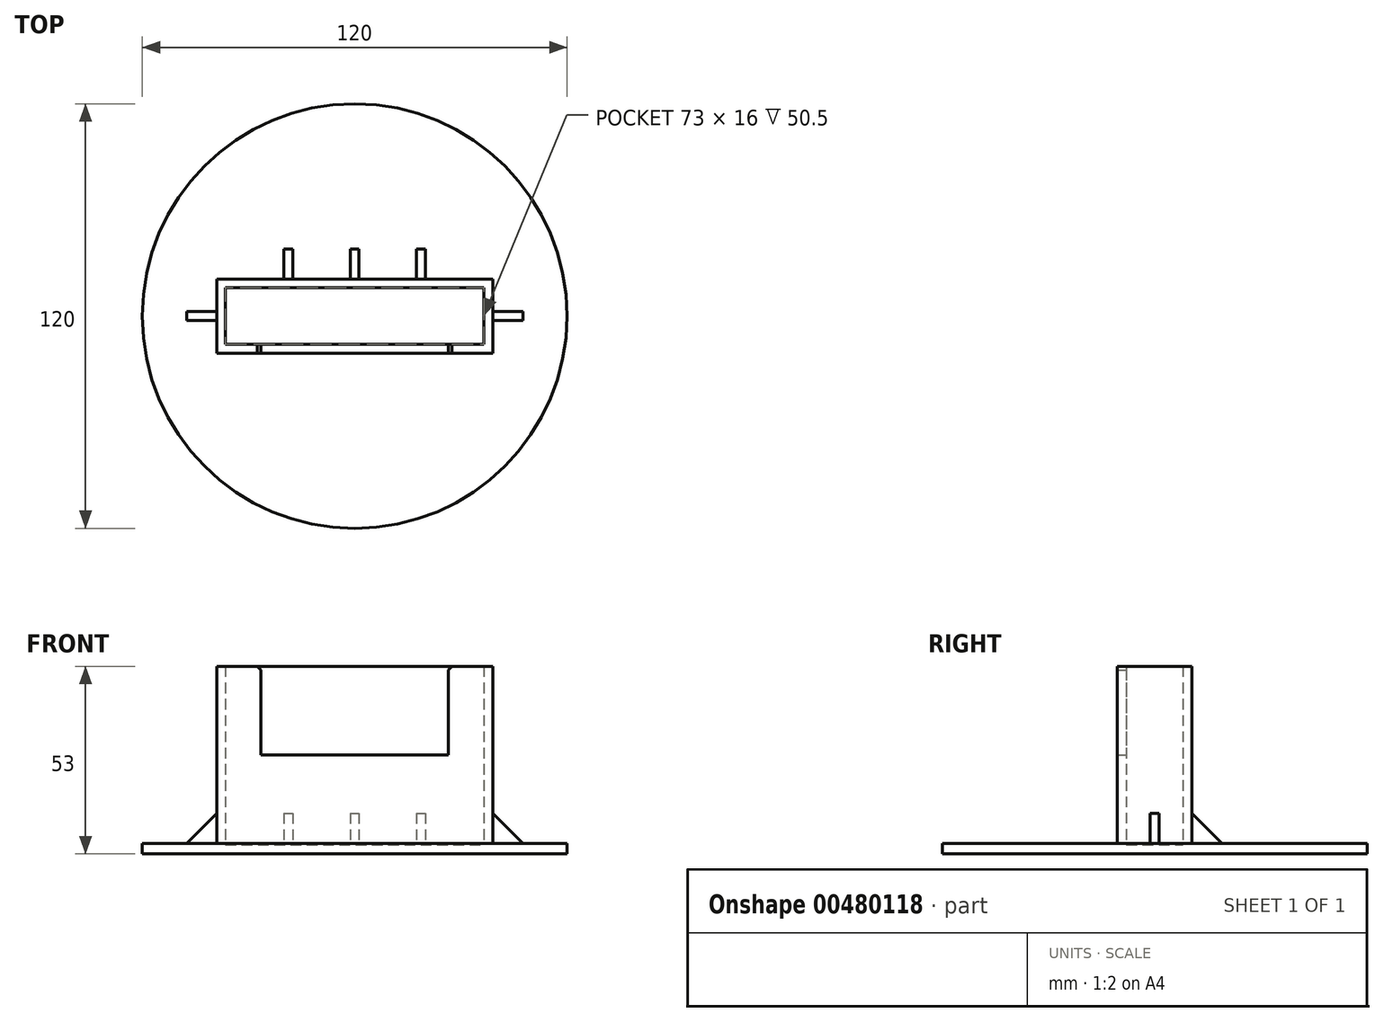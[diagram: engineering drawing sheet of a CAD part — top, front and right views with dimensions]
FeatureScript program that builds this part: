
annotation { "Feature Type Name" : "Feature", "Feature Type Description" : "" }
export const myFeature = defineFeature(function(context is Context, id is Id, definition is map)
    precondition{}
    {
        {
            var Q0;
            Q0=qCreatedBy(makeId("Top.planeOp"),FACE);
            var sketch = newSketch(context, id + "F0", { "sketchPlane" : qUnion([Q0])});
            skCircle(sketch, "E0", {"center": v(0, 0) * mm, "radius": 60 * mm});
            skLineSegment(sketch, "E1.bottom", {"start": v(39, 10.5) * mm, "end": v(-39, 10.5) * mm});
            skLineSegment(sketch, "E1.top", {"start": v(39, -10.5) * mm, "end": v(-39, -10.5) * mm});
            skLineSegment(sketch, "E1.left", {"start": v(39, 10.5) * mm, "end": v(39, -10.5) * mm});
            skLineSegment(sketch, "E1.right", {"start": v(-39, 10.5) * mm, "end": v(-39, -10.5) * mm});
            skPoint(sketch, "E2.endSnap0", {"position": v(0, 10.5) * mm});
            skPoint(sketch, "E3.endSnap0", {"position": v(39, 0) * mm});
            skLineSegment(sketch, "E4.0", {"start": v(-37.5, 1.25) * mm, "end": v(-47.5, 1.25) * mm});
            skLineSegment(sketch, "E5.0", {"start": v(-37.5, -1.25) * mm, "end": v(-47.5, -1.25) * mm});
            skLineSegment(sketch, "E6", {"start": v(-47.5, 1.25) * mm, "end": v(-47.5, -1.25) * mm});
            skLineSegment(sketch, "E7.0", {"start": v(-17.5, 9) * mm, "end": v(-17.5, 19) * mm});
            skLineSegment(sketch, "E8.0", {"start": v(-20, 9) * mm, "end": v(-20, 19) * mm});
            skLineSegment(sketch, "E9.0", {"start": v(1.25, 9) * mm, "end": v(1.25, 19) * mm});
            skLineSegment(sketch, "E10.0", {"start": v(-1.25, 9) * mm, "end": v(-1.25, 19) * mm});
            skLineSegment(sketch, "E11.0", {"start": v(20, 9) * mm, "end": v(20, 19) * mm});
            skLineSegment(sketch, "E12.0", {"start": v(17.5, 9) * mm, "end": v(17.5, 19) * mm});
            skLineSegment(sketch, "E13.0", {"start": v(37.5, -1.25) * mm, "end": v(47.5, -1.25) * mm});
            skLineSegment(sketch, "E14.0", {"start": v(37.5, 1.25) * mm, "end": v(47.5, 1.25) * mm});
            skLineSegment(sketch, "E15", {"start": v(-20, 19) * mm, "end": v(-17.5, 19) * mm});
            skLineSegment(sketch, "E16", {"start": v(-1.25, 19) * mm, "end": v(1.25, 19) * mm});
            skLineSegment(sketch, "E17", {"start": v(17.5, 19) * mm, "end": v(20, 19) * mm});
            skLineSegment(sketch, "E18", {"start": v(47.5, 1.25) * mm, "end": v(47.5, -1.25) * mm});
            skSolve(sketch);
        }
        {
            var Q0;
            Q0=qCreatedBy(makeId("Front.planeOp"),FACE);
            var sketch = newSketch(context, id + "F1", { "sketchPlane" : qUnion([Q0])});
            skPoint(sketch, "E19.middle", {"position": v(0, 0) * mm});
            skLineSegment(sketch, "E20", {"start": v(26.5, 25) * mm, "end": v(-26.5, 25) * mm});
            skLineSegment(sketch, "E21", {"start": v(-26.5, 25) * mm, "end": v(-26.5, 75) * mm});
            skLineSegment(sketch, "E22", {"start": v(26.5, 25) * mm, "end": v(26.5, 75) * mm});
            skLineSegment(sketch, "E23", {"start": v(-26.5, 75) * mm, "end": v(26.5, 75) * mm});
            skSolve(sketch);
        }
        {
            var Q0;
            Q0 = qSketchRegion(id + "F0", true);
            var Q1;
            Q1=makeQuery(id+"F0.imprint","IMPRINT",FACE,{"disambiguationData":[TD([[makeQuery(id+"F0.imprint","IMPRINT",EDGE,{"derivedFrom":sQuery(id+"F0.wireOp",EDGE,"E1.bottom")}),1.0]])]});
            var Q2;
            {var subQ0=sQuery(id+"F0.wireOp",EDGE,"E4.0");Q2=makeQuery(id+"F0.imprint","IMPRINT",FACE,{"disambiguationData":[TD([[makeQuery(id+"F0.imprint","IMPRINT",EDGE,{"derivedFrom":subQ0}),1.0]])]});}
            var Q3;
            {var subQ0=sQuery(id+"F0.wireOp",EDGE,"E7.0");Q3=makeQuery(id+"F0.imprint","IMPRINT",FACE,{"disambiguationData":[TD([[makeQuery(id+"F0.imprint","IMPRINT",EDGE,{"derivedFrom":subQ0}),1.0]])]});}
            var Q4;
            {var subQ0=sQuery(id+"F0.wireOp",EDGE,"E9.0");Q4=makeQuery(id+"F0.imprint","IMPRINT",FACE,{"disambiguationData":[TD([[makeQuery(id+"F0.imprint","IMPRINT",EDGE,{"derivedFrom":subQ0}),1.0]])]});}
            var Q5;
            {var subQ0=sQuery(id+"F0.wireOp",EDGE,"E11.0");Q5=makeQuery(id+"F0.imprint","IMPRINT",FACE,{"disambiguationData":[TD([[makeQuery(id+"F0.imprint","IMPRINT",EDGE,{"derivedFrom":subQ0}),1.0]])]});}
            var Q6;
            {var subQ0=sQuery(id+"F0.wireOp",EDGE,"E13.0");Q6=makeQuery(id+"F0.imprint","IMPRINT",FACE,{"disambiguationData":[TD([[makeQuery(id+"F0.imprint","IMPRINT",EDGE,{"derivedFrom":subQ0}),1.0]])]});}
            extrude(context, id + "F2", {"entities" : qUnion([Q0, Q1, Q2, Q3, Q4, Q5, Q6]), "oppositeDirection" : true, "depth" : 3 * mm});
        }
        {
            var Q0;
            Q0=makeQuery(id+"F0.imprint","IMPRINT",FACE,{"disambiguationData":[TD([[makeQuery(id+"F0.imprint","IMPRINT",EDGE,{"derivedFrom":sQuery(id+"F0.wireOp",EDGE,"E1.bottom")}),1.0]])]});
            extrude(context, id + "F3", {"entities" : qUnion([Q0]), "operationType" : NewBodyOperationType.ADD, "depth" : 50 * mm});
        }
        {
            var Q0;
            Q0=makeQuery(id+"F3.opExtrude","CAP_FACE",FACE,{"disambiguationData":[OSD([sQuery(id+"F0.wireOp",EDGE,"E1.bottom"),sQuery(id+"F0.wireOp",EDGE,"E1.top"),sQuery(id+"F0.wireOp",EDGE,"E1.left"),sQuery(id+"F0.wireOp",EDGE,"E1.right")])],"isStart":false});
            shell(context, id + "F4", {"entities" : qUnion([Q0]), "thickness" : 2.5 * mm});
        }
        {
            var Q0;
            {var subQ0=sQuery(id+"F0.wireOp",EDGE,"E4.0");Q0=makeQuery(id+"F0.imprint","IMPRINT",FACE,{"disambiguationData":[TD([[makeQuery(id+"F0.imprint","IMPRINT",EDGE,{"derivedFrom":subQ0}),1.0]])]});}
            var Q1;
            {var subQ0=sQuery(id+"F0.wireOp",EDGE,"E7.0");Q1=makeQuery(id+"F0.imprint","IMPRINT",FACE,{"disambiguationData":[TD([[makeQuery(id+"F0.imprint","IMPRINT",EDGE,{"derivedFrom":subQ0}),1.0]])]});}
            var Q2;
            {var subQ0=sQuery(id+"F0.wireOp",EDGE,"E9.0");Q2=makeQuery(id+"F0.imprint","IMPRINT",FACE,{"disambiguationData":[TD([[makeQuery(id+"F0.imprint","IMPRINT",EDGE,{"derivedFrom":subQ0}),1.0]])]});}
            var Q3;
            {var subQ0=sQuery(id+"F0.wireOp",EDGE,"E11.0");Q3=makeQuery(id+"F0.imprint","IMPRINT",FACE,{"disambiguationData":[TD([[makeQuery(id+"F0.imprint","IMPRINT",EDGE,{"derivedFrom":subQ0}),1.0]])]});}
            var Q4;
            {var subQ0=sQuery(id+"F0.wireOp",EDGE,"E13.0");Q4=makeQuery(id+"F0.imprint","IMPRINT",FACE,{"disambiguationData":[TD([[makeQuery(id+"F0.imprint","IMPRINT",EDGE,{"derivedFrom":subQ0}),1.0]])]});}
            extrude(context, id + "F5", {"entities" : qUnion([Q0, Q1, Q2, Q3, Q4]), "operationType" : NewBodyOperationType.ADD, "depth" : 10 * mm});
        }
        {
            var Q0;
            Q0=makeQuery(id+"F5.opExtrude","CAP_EDGE",EDGE,{"disambiguationData":[OSD([sQuery(id+"F0.wireOp",EDGE,"E18")])],"isStart":false});
            var Q1;
            Q1=makeQuery(id+"F5.opExtrude","CAP_EDGE",EDGE,{"disambiguationData":[OSD([sQuery(id+"F0.wireOp",EDGE,"E17")])],"isStart":false});
            var Q2;
            Q2=makeQuery(id+"F5.opExtrude","CAP_EDGE",EDGE,{"disambiguationData":[OSD([sQuery(id+"F0.wireOp",EDGE,"E16")])],"isStart":false});
            var Q3;
            Q3=makeQuery(id+"F5.opExtrude","CAP_EDGE",EDGE,{"disambiguationData":[OSD([sQuery(id+"F0.wireOp",EDGE,"E15")])],"isStart":false});
            var Q4;
            Q4=makeQuery(id+"F5.opExtrude","CAP_EDGE",EDGE,{"disambiguationData":[OSD([sQuery(id+"F0.wireOp",EDGE,"E6")])],"isStart":false});
            chamfer(context, id + "F6", {"entities" : qUnion([Q0, Q1, Q2, Q3, Q4]), "width" : 10 * mm, "tangentPropagation" : true});
        }
        {
            var Q0;
            Q0=makeQuery(id+"F1.imprint","IMPRINT",FACE,{"disambiguationData":[TD([[makeQuery(id+"F1.imprint","IMPRINT",EDGE,{"derivedFrom":sQuery(id+"F1.wireOp",EDGE,"E20")}),-1.0]])]});
            extrude(context, id + "F7", {"entities" : qUnion([Q0]), "operationType" : NewBodyOperationType.REMOVE, "depth" : 25 * mm});
        }
        {
            var Q0;
            Q0=makeQuery(id+"F7.boolean.opBoolean","INTERSECT",EDGE,{"derivedFrom":[makeQuery(id+"F3.opExtrude","CAP_FACE",FACE,{"disambiguationData":[OSD([sQuery(id+"F0.wireOp",EDGE,"E1.bottom"),sQuery(id+"F0.wireOp",EDGE,"E1.top"),sQuery(id+"F0.wireOp",EDGE,"E1.left"),sQuery(id+"F0.wireOp",EDGE,"E1.right")])],"isStart":false}),makeQuery(id+"F7.opExtrude","SWEPT_FACE",FACE,{"disambiguationData":[OSD([sQuery(id+"F1.wireOp",EDGE,"E21")])]})]});
            var Q1;
            Q1=makeQuery(id+"F7.boolean.opBoolean","INTERSECT",EDGE,{"derivedFrom":[makeQuery(id+"F3.opExtrude","CAP_FACE",FACE,{"disambiguationData":[OSD([sQuery(id+"F0.wireOp",EDGE,"E1.bottom"),sQuery(id+"F0.wireOp",EDGE,"E1.top"),sQuery(id+"F0.wireOp",EDGE,"E1.left"),sQuery(id+"F0.wireOp",EDGE,"E1.right")])],"isStart":false}),makeQuery(id+"F7.opExtrude","SWEPT_FACE",FACE,{"disambiguationData":[OSD([sQuery(id+"F1.wireOp",EDGE,"E22")])]})]});
            chamfer(context, id + "F8", {"entities" : qUnion([Q0, Q1]), "width" : 1 * mm, "tangentPropagation" : true});
        }
    });
